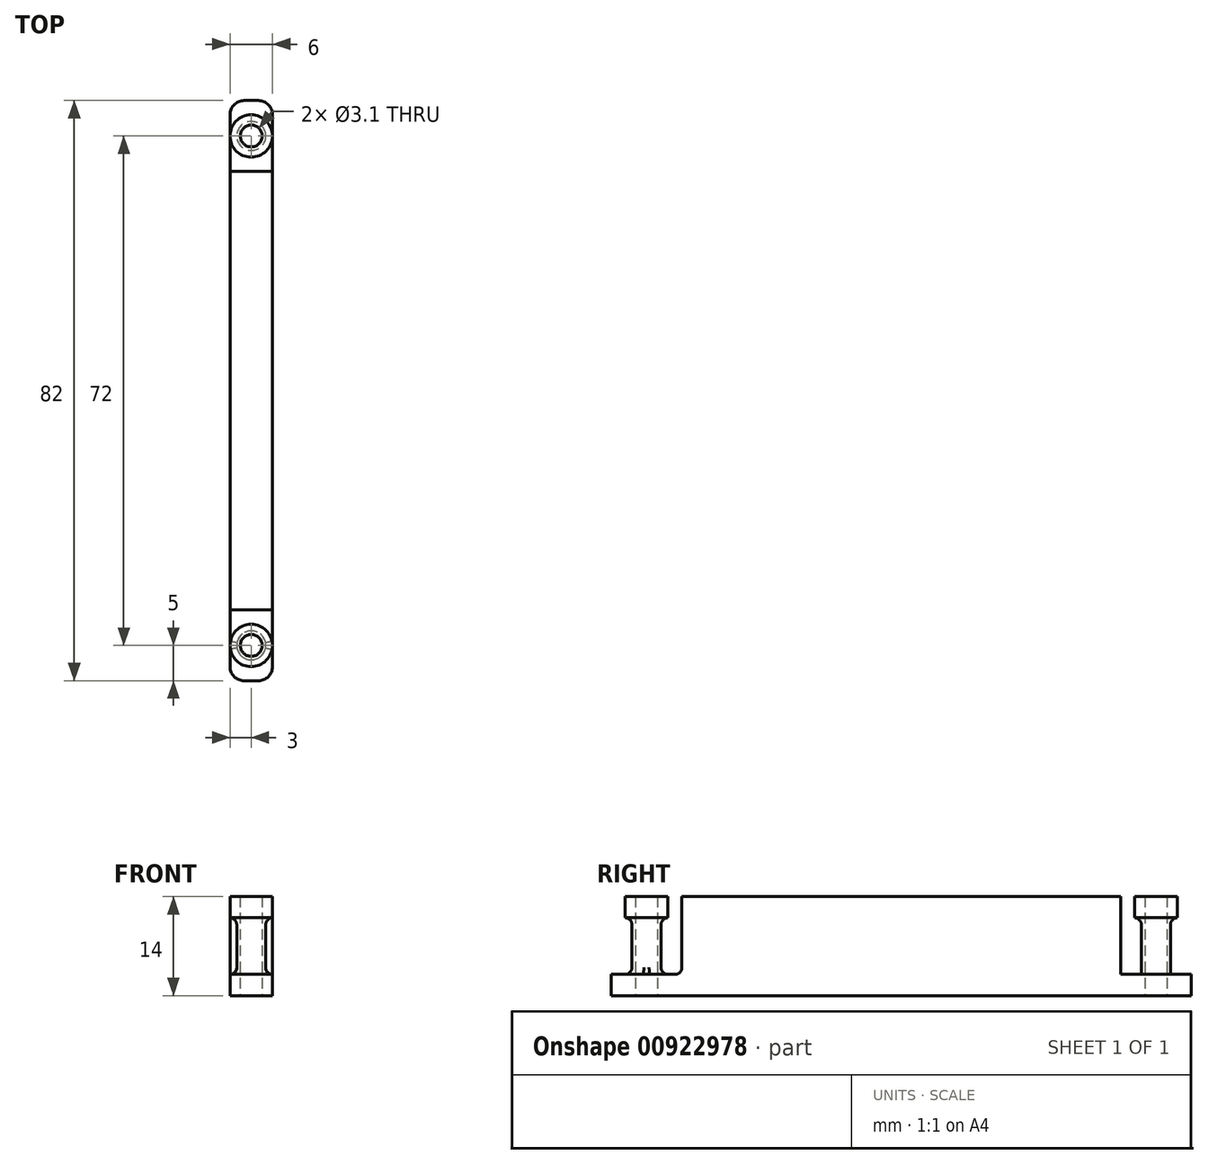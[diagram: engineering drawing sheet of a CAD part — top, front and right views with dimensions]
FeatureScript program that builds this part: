
annotation { "Feature Type Name" : "Feature", "Feature Type Description" : "" }
export const myFeature = defineFeature(function(context is Context, id is Id, definition is map)
    precondition{}
    {
        {
            var Q0;
            Q0=qCreatedBy(makeId("Top.planeOp"),FACE);
            var sketch = newSketch(context, id + "F0", { "sketchPlane" : qUnion([Q0])});
            skCircle(sketch, "E0", {"center": v(0, 0) * mm, "radius": 1.55 * mm});
            skCircle(sketch, "E1", {"center": v(0, -72) * mm, "radius": 1.55 * mm});
            skLineSegment(sketch, "E2.bottom", {"start": v(-1, -77) * mm, "end": v(1, -77) * mm});
            skLineSegment(sketch, "E2.top", {"start": v(-1, 5) * mm, "end": v(1, 5) * mm});
            skLineSegment(sketch, "E2.left", {"start": v(-3, -75) * mm, "end": v(-3, 3) * mm});
            skLineSegment(sketch, "E2.right", {"start": v(3, -75) * mm, "end": v(3, 3) * mm});
            skPoint(sketch, "E3.visualSharp", {"position": v(3, 5) * mm});
            skArc(sketch, "E3.filletArc", {"start": v(3, 3) * mm, "mid": v(2.41, 4.41) * mm, "end": v(1, 5) * mm});
            skPoint(sketch, "E4.visualSharp", {"position": v(-3, 5) * mm});
            skArc(sketch, "E4.filletArc", {"start": v(-1, 5) * mm, "mid": v(-2.41, 4.41) * mm, "end": v(-3, 3) * mm});
            skPoint(sketch, "E5.visualSharp", {"position": v(-3, -77) * mm});
            skArc(sketch, "E5.filletArc", {"start": v(-3, -75) * mm, "mid": v(-2.41, -76.41) * mm, "end": v(-1, -77) * mm});
            skPoint(sketch, "E6.visualSharp", {"position": v(3, -77) * mm});
            skArc(sketch, "E6.filletArc", {"start": v(1, -77) * mm, "mid": v(2.41, -76.41) * mm, "end": v(3, -75) * mm});
            skSolve(sketch);
        }
        {
            var Q0;
            Q0=makeQuery(id+"F0.imprint","IMPRINT",FACE,{"disambiguationData":[TD([[makeQuery(id+"F0.imprint","IMPRINT",EDGE,{"derivedFrom":sQuery(id+"F0.wireOp",EDGE,"E0")}),-1.0]])]});
            extrude(context, id + "F1", {"entities" : qUnion([Q0]), "depth" : 3 * mm, "offsetDistance" : 25 * mm});
        }
        {
            var Q0;
            Q0=makeQuery(id+"F1.opExtrude","CAP_FACE",FACE,{"disambiguationData":[OSD([sQuery(id+"F0.wireOp",EDGE,"E0"),sQuery(id+"F0.wireOp",EDGE,"E1"),sQuery(id+"F0.wireOp",EDGE,"E2.bottom"),sQuery(id+"F0.wireOp",EDGE,"E2.top"),sQuery(id+"F0.wireOp",EDGE,"E2.left"),sQuery(id+"F0.wireOp",EDGE,"E2.right")])],"isStart":false});
            var sketch = newSketch(context, id + "F2", { "sketchPlane" : qUnion([Q0])});
            skLineSegment(sketch, "E7.bottom", {"start": v(3, -5) * mm, "end": v(-3, -5) * mm});
            skLineSegment(sketch, "E7.top", {"start": v(3, -67) * mm, "end": v(-3, -67) * mm});
            skLineSegment(sketch, "E7.left", {"start": v(3, -5) * mm, "end": v(3, -67) * mm});
            skLineSegment(sketch, "E7.right", {"start": v(-3, -5) * mm, "end": v(-3, -67) * mm});
            skCircle(sketch, "E8.0", {"center": v(0, -72) * mm, "radius": 1.55 * mm, "construction": true});
            skLineSegment(sketch, "E9.0.0", {"start": v(1, 5) * mm, "end": v(-1, 5) * mm});
            skArc(sketch, "E9.0.1", {"start": v(-1, 5) * mm, "mid": v(-2.41, 4.41) * mm, "end": v(-3, 3) * mm});
            skLineSegment(sketch, "E9.0.2", {"start": v(-3, 3) * mm, "end": v(-3, -75) * mm});
            skArc(sketch, "E9.0.3", {"start": v(-3, -75) * mm, "mid": v(-2.41, -76.41) * mm, "end": v(-1, -77) * mm});
            skLineSegment(sketch, "E9.0.4", {"start": v(-1, -77) * mm, "end": v(1, -77) * mm});
            skArc(sketch, "E9.0.5", {"start": v(1, -77) * mm, "mid": v(2.41, -76.41) * mm, "end": v(3, -75) * mm});
            skLineSegment(sketch, "E9.0.6", {"start": v(3, -75) * mm, "end": v(3, 3) * mm});
            skArc(sketch, "E9.0.7", {"start": v(3, 3) * mm, "mid": v(2.41, 4.41) * mm, "end": v(1, 5) * mm});
            skCircle(sketch, "E10.0", {"center": v(0, 0) * mm, "radius": 1.55 * mm});
            skCircle(sketch, "E11", {"center": v(0, 0) * mm, "radius": 2.05 * mm});
            skCircle(sketch, "E12", {"center": v(0, -72) * mm, "radius": 2.05 * mm});
            skSolve(sketch);
        }
        {
            var Q0;
            {var subQ0=sQuery(id+"F2.wireOp",EDGE,"E7.bottom");Q0=makeQuery(id+"F2.imprint","IMPRINT",FACE,{"disambiguationData":[TD([[makeQuery(id+"F2.imprint","IMPRINT",EDGE,{"derivedFrom":subQ0}),1.0]])]});}
            var Q1;
            Q1=makeQuery(id+"F2.imprint","IMPRINT",FACE,{"disambiguationData":[TD([[makeQuery(id+"F2.imprint","IMPRINT",EDGE,{"derivedFrom":sQuery(id+"F2.wireOp",EDGE,"E10.0")}),-1.0]])]});
            var Q2;
            Q2=makeQuery(id+"F2.imprint","IMPRINT",FACE,{"disambiguationData":[TD([[makeQuery(id+"F2.imprint","IMPRINT",EDGE,{"derivedFrom":sQuery(id+"F2.wireOp",EDGE,"E12")}),1.0]])]});
            extrude(context, id + "F3", {"entities" : qUnion([Q0, Q1, Q2]), "operationType" : NewBodyOperationType.ADD, "depth" : 11 * mm, "offsetDistance" : 25 * mm});
        }
        {
            var Q0;
            Q0=makeQuery(id+"F3.opExtrude","CAP_EDGE",EDGE,{"disambiguationData":[OSD([sQuery(id+"F2.wireOp",EDGE,"E7.bottom")])],"isStart":true});
            var Q1;
            Q1=makeQuery(id+"F3.opExtrude","CAP_EDGE",EDGE,{"disambiguationData":[OSD([sQuery(id+"F2.wireOp",EDGE,"E7.top")])],"isStart":true});
            fillet(context, id + "F4", {"entities" : qUnion([Q0, Q1]), "radius" : 1 * mm, "tangentPropagation" : true, "allowEdgeOverflow" : false});
        }
        {
            var Q0;
            Q0=makeQuery(id+"F3.opExtrude","CAP_FACE",FACE,{"disambiguationData":[OSD([sQuery(id+"F2.wireOp",EDGE,"E7.bottom"),sQuery(id+"F2.wireOp",EDGE,"E7.top"),sQuery(id+"F2.wireOp",EDGE,"E9.0.2"),sQuery(id+"F2.wireOp",EDGE,"E9.0.6")])],"isStart":false});
            var sketch = newSketch(context, id + "F5", { "sketchPlane" : qUnion([Q0])});
            skCircle(sketch, "E13", {"center": v(0, 0) * mm, "radius": 3 * mm});
            skLineSegment(sketch, "E14.0", {"start": v(-3, -4) * mm, "end": v(-3, 3) * mm, "construction": true});
            skCircle(sketch, "E15.0", {"center": v(0, -72) * mm, "radius": 1.55 * mm});
            skCircle(sketch, "E16", {"center": v(0, -72) * mm, "radius": 3 * mm});
            skCircle(sketch, "E17.0", {"center": v(0, 0) * mm, "radius": 1.55 * mm});
            skSolve(sketch);
        }
        {
            var Q0;
            Q0 = qSketchRegion(id + "F5", true);
            extrude(context, id + "F6", {"entities" : qUnion([Q0]), "operationType" : NewBodyOperationType.ADD, "oppositeDirection" : true, "depth" : 3 * mm, "offsetDistance" : 25 * mm});
        }
        {
            var Q0;
            Q0=makeQuery(id+"F6.boolean.opBoolean","INTERSECT",EDGE,{"derivedFrom":[makeQuery(id+"F3.opExtrude","SWEPT_FACE",FACE,{"disambiguationData":[OSD([sQuery(id+"F2.wireOp",EDGE,"E11")])]}),makeQuery(id+"F6.opExtrude","CAP_FACE",FACE,{"disambiguationData":[OSD([sQuery(id+"F5.wireOp",EDGE,"E13"),sQuery(id+"F5.wireOp",EDGE,"E17.0")])],"isStart":false})]});
            var Q1;
            Q1=makeQuery(id+"F3.opExtrude","CAP_EDGE",EDGE,{"disambiguationData":[OSD([sQuery(id+"F2.wireOp",EDGE,"E11")])],"isStart":true});
            var Q2;
            Q2=makeQuery(id+"F3.opExtrude","CAP_EDGE",EDGE,{"disambiguationData":[OSD([sQuery(id+"F2.wireOp",EDGE,"E12")])],"isStart":true});
            var Q3;
            Q3=makeQuery(id+"F6.boolean.opBoolean","INTERSECT",EDGE,{"derivedFrom":[makeQuery(id+"F3.opExtrude","SWEPT_FACE",FACE,{"disambiguationData":[OSD([sQuery(id+"F2.wireOp",EDGE,"E12")])]}),makeQuery(id+"F6.opExtrude","CAP_FACE",FACE,{"disambiguationData":[OSD([sQuery(id+"F5.wireOp",EDGE,"E15.0"),sQuery(id+"F5.wireOp",EDGE,"E16")])],"isStart":false})]});
            fillet(context, id + "F7", {"entities" : qUnion([Q0, Q1, Q2, Q3]), "radius" : 1 * mm, "tangentPropagation" : true, "allowEdgeOverflow" : false});
        }
    });
